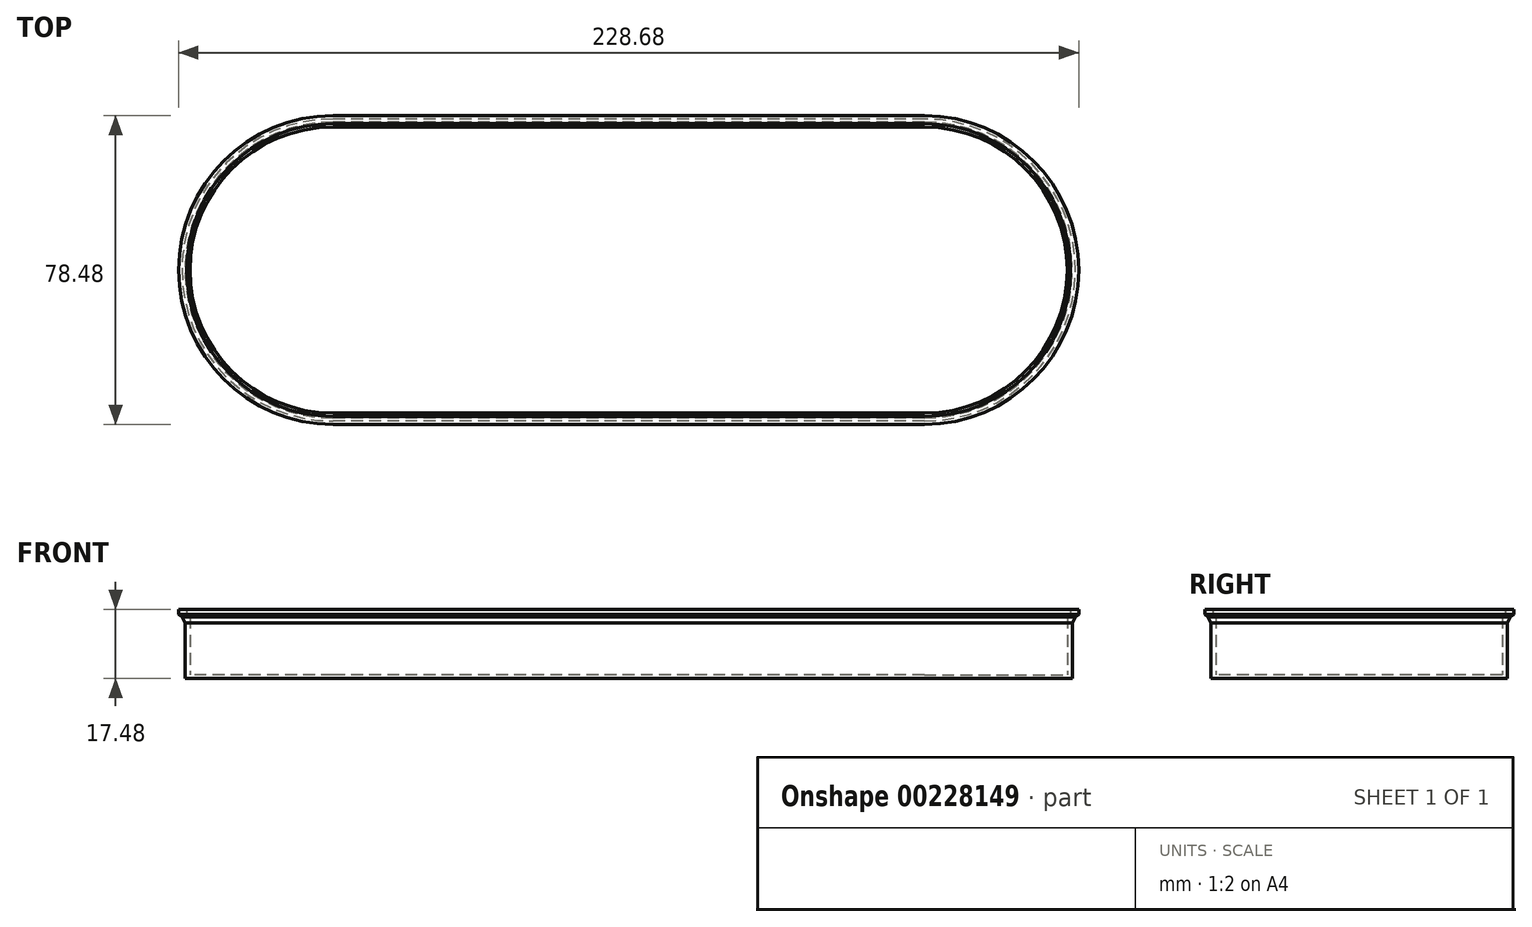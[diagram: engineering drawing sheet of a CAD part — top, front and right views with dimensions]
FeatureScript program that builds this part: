
annotation { "Feature Type Name" : "Feature", "Feature Type Description" : "" }
export const myFeature = defineFeature(function(context is Context, id is Id, definition is map)
    precondition{}
    {
        {
            assignVariable(context, id + "F0", {"name" : "Height", "anyValue" : 15});
        }
        {
            assignVariable(context, id + "F1", {"name" : "WallThickness", "anyValue" : 1.24});
        }
        {
            var Q0;
            Q0=qCreatedBy(makeId("Top.planeOp"),FACE);
            var sketch = newSketch(context, id + "F2", { "sketchPlane" : qUnion([Q0])});
            skLineSegment(sketch, "E0.bottom", {"start": v(75.1, 37.6) * mm, "end": v(-75.1, 37.6) * mm});
            skLineSegment(sketch, "E0.top", {"start": v(75.1, -37.6) * mm, "end": v(-75.1, -37.6) * mm});
            skLineSegment(sketch, "E0.left", {"start": v(75.1, 37.6) * mm, "end": v(75.1, -37.6) * mm});
            skLineSegment(sketch, "E0.right", {"start": v(-75.1, 37.6) * mm, "end": v(-75.1, -37.6) * mm});
            skPoint(sketch, "E0.middle", {"position": v(0, 0) * mm});
            skCircle(sketch, "E1", {"center": v(-75.1, 0) * mm, "radius": 37.6 * mm});
            skCircle(sketch, "E2", {"center": v(75.1, 0) * mm, "radius": 37.6 * mm});
            skSolve(sketch);
        }
        {
            var Q0;
            Q0=makeQuery(id+"F2.imprint","IMPRINT",FACE,{"disambiguationData":[TD([[makeQuery(id+"F2.imprint","IMPRINT",EDGE,{"derivedFrom":sQuery(id+"F2.wireOp",EDGE,"E0.bottom")}),1.0]])]});
            var Q1;
            {var subQ0=sQuery(id+"F2.wireOp",EDGE,"E0.left");Q1=makeQuery(id+"F2.imprint","IMPRINT",FACE,{"disambiguationData":[TD([[makeQuery(id+"F2.imprint","IMPRINT",EDGE,{"derivedFrom":subQ0}),-1.0]])]});}
            var Q2;
            {var subQ0=sQuery(id+"F2.wireOp",EDGE,"E0.right");Q2=makeQuery(id+"F2.imprint","IMPRINT",FACE,{"disambiguationData":[TD([[makeQuery(id+"F2.imprint","IMPRINT",EDGE,{"derivedFrom":subQ0}),-1.0]])]});}
            var Q3;
            {var subQ0=sQuery(id+"F2.wireOp",EDGE,"E0.right");Q3=makeQuery(id+"F2.imprint","IMPRINT",FACE,{"disambiguationData":[TD([[makeQuery(id+"F2.imprint","IMPRINT",EDGE,{"derivedFrom":subQ0}),1.0]])]});}
            var Q4;
            {var subQ0=sQuery(id+"F2.wireOp",EDGE,"E0.left");Q4=makeQuery(id+"F2.imprint","IMPRINT",FACE,{"disambiguationData":[TD([[makeQuery(id+"F2.imprint","IMPRINT",EDGE,{"derivedFrom":subQ0}),1.0]])]});}
            extrude(context, id + "F3", {"entities" : qUnion([Q0, Q1, Q2, Q3, Q4]), "offsetDistance" : 25 * mm, "depth" : (getVariable(context, 'Height')) * mm});
        }
        {
            var Q0;
            Q0=makeQuery(id+"F3.opExtrude","CAP_FACE",FACE,{"disambiguationData":[OSD([sQuery(id+"F2.wireOp",EDGE,"E0.bottom"),sQuery(id+"F2.wireOp",EDGE,"E0.top"),sQuery(id+"F2.wireOp",EDGE,"E0.left"),sQuery(id+"F2.wireOp",EDGE,"E0.right")])],"isStart":false});
            cPlane(context, id + "F4", {"entities" : qUnion([Q0]), "cplaneType" : CPlaneType.OFFSET, "offset" : (getVariable(context, 'WallThickness')) * mm, "width" : 150 * mm, "height" : 150 * mm});
        }
        {
            var Q0;
            Q0=qCreatedBy(id+"F4.planeOp",FACE);
            var sketch = newSketch(context, id + "F5", { "sketchPlane" : qUnion([Q0])});
            skLineSegment(sketch, "E3.0.0", {"start": v(-75.1, -37.6) * mm, "end": v(75.1, -37.6) * mm, "construction": true});
            skArc(sketch, "E3.0.1", {"start": v(75.1, -37.6) * mm, "mid": v(112.7, 0) * mm, "end": v(75.1, 37.6) * mm, "construction": true});
            skLineSegment(sketch, "E3.0.2", {"start": v(75.1, 37.6) * mm, "end": v(-75.1, 37.6) * mm, "construction": true});
            skArc(sketch, "E3.0.3", {"start": v(-75.1, 37.6) * mm, "mid": v(-112.7, 0) * mm, "end": v(-75.1, -37.6) * mm, "construction": true});
            skArc(sketch, "E4.0", {"start": v(-75.1, 38) * mm, "mid": v(-113.1, 0) * mm, "end": v(-75.1, -38) * mm, "construction": true});
            skLineSegment(sketch, "E4.1", {"start": v(75.1, 38) * mm, "end": v(-75.1, 38) * mm, "construction": true});
            skArc(sketch, "E4.2", {"start": v(75.1, -38) * mm, "mid": v(113.1, 0) * mm, "end": v(75.1, 38) * mm, "construction": true});
            skLineSegment(sketch, "E4.3", {"start": v(-75.1, -38) * mm, "end": v(75.1, -38) * mm, "construction": true});
            skArc(sketch, "E5.0", {"start": v(-75.1, 39.24) * mm, "mid": v(-114.34, 0) * mm, "end": v(-75.1, -39.24) * mm});
            skLineSegment(sketch, "E5.1", {"start": v(75.1, 39.24) * mm, "end": v(-75.1, 39.24) * mm});
            skArc(sketch, "E5.2", {"start": v(75.1, -39.24) * mm, "mid": v(114.34, 0) * mm, "end": v(75.1, 39.24) * mm});
            skLineSegment(sketch, "E5.3", {"start": v(-75.1, -39.24) * mm, "end": v(75.1, -39.24) * mm});
            skSolve(sketch);
        }
        {
            var Q1;
            Q1=makeQuery(id+"F3.opExtrude","CAP_FACE",FACE,{"disambiguationData":[OSD([sQuery(id+"F2.wireOp",EDGE,"E0.bottom"),sQuery(id+"F2.wireOp",EDGE,"E0.top"),sQuery(id+"F2.wireOp",EDGE,"E1"),sQuery(id+"F2.wireOp",EDGE,"E2")])],"isStart":false});
            var Q2;
            Q2=makeQuery(id+"F5.imprint","IMPRINT",FACE,{"disambiguationData":[TD([[makeQuery(id+"F5.imprint","IMPRINT",EDGE,{"derivedFrom":sQuery(id+"F5.wireOp",EDGE,"E5.0")}),1.0]])]});
            loft(context, id + "F6", {"operationType" : NewBodyOperationType.ADD, "sheetProfilesArray" : [{ "sheetProfileEntities" : qUnion([Q1]) }, { "sheetProfileEntities" : qUnion([Q2]) }]});
        }
        {
            var Q0;
            Q0=makeQuery(id+"F6.opLoft","CAP_FACE",FACE,{"disambiguationData":[OSD([makeQuery(id+"F5.imprint","IMPRINT",FACE,{"disambiguationData":[TD([[makeQuery(id+"F5.imprint","IMPRINT",EDGE,{"derivedFrom":sQuery(id+"F5.wireOp",EDGE,"E5.0")}),1.0]])]})])],"isStart":true});
            shell(context, id + "F7", {"entities" : qUnion([Q0]), "thickness" : (getVariable(context, 'WallThickness')) * mm});
        }
        {
            var Q0;
            Q0=makeQuery(id+"F6.opLoft","CAP_FACE",FACE,{"disambiguationData":[OSD([makeQuery(id+"F5.imprint","IMPRINT",FACE,{"disambiguationData":[TD([[makeQuery(id+"F5.imprint","IMPRINT",EDGE,{"derivedFrom":sQuery(id+"F5.wireOp",EDGE,"E5.0")}),1.0]])]})])],"isStart":true});
            extrude(context, id + "F8", {"entities" : qUnion([Q0]), "operationType" : NewBodyOperationType.ADD, "offsetDistance" : 25 * mm, "depth" : (getVariable(context, 'WallThickness')) * mm});
        }
        {
            var Q0;
            {var subQ0=sQuery(id+"F2.wireOp",EDGE,"E0.right");Q0=makeQuery(id+"F6.boolean.opBoolean","MERGE",EDGE,{"derivedFrom":[makeQuery(id+"F3.opExtrude","CAP_EDGE",EDGE,{"disambiguationData":[OSD([subQ0])],"isStart":false}),makeQuery(id+"F6.opLoft","MID_CAP_EDGE",EDGE,{"disambiguationData":[OSD([sQuery(id+"F2.wireOp",EDGE,"E0.bottom"),sQuery(id+"F2.wireOp",EDGE,"E0.top"),subQ0])],"capPos":1.0})]});}
            var Q1;
            {var subQ0=sQuery(id+"F2.wireOp",EDGE,"E0.top");Q1=makeQuery(id+"F6.boolean.opBoolean","MERGE",EDGE,{"derivedFrom":[makeQuery(id+"F3.opExtrude","CAP_EDGE",EDGE,{"disambiguationData":[OSD([subQ0])],"isStart":false}),makeQuery(id+"F6.opLoft","MID_CAP_EDGE",EDGE,{"disambiguationData":[OSD([subQ0,sQuery(id+"F2.wireOp",EDGE,"E0.left"),sQuery(id+"F2.wireOp",EDGE,"E0.right")])],"capPos":1.0})]});}
            var Q2;
            {var subQ0=sQuery(id+"F2.wireOp",EDGE,"E0.left");Q2=makeQuery(id+"F6.boolean.opBoolean","MERGE",EDGE,{"derivedFrom":[makeQuery(id+"F3.opExtrude","CAP_EDGE",EDGE,{"disambiguationData":[OSD([subQ0])],"isStart":false}),makeQuery(id+"F6.opLoft","MID_CAP_EDGE",EDGE,{"disambiguationData":[OSD([sQuery(id+"F2.wireOp",EDGE,"E0.bottom"),sQuery(id+"F2.wireOp",EDGE,"E0.top"),subQ0])],"capPos":1.0})]});}
            var Q3;
            {var subQ0=sQuery(id+"F2.wireOp",EDGE,"E0.bottom");Q3=makeQuery(id+"F6.boolean.opBoolean","MERGE",EDGE,{"derivedFrom":[makeQuery(id+"F3.opExtrude","CAP_EDGE",EDGE,{"disambiguationData":[OSD([subQ0])],"isStart":false}),makeQuery(id+"F6.opLoft","MID_CAP_EDGE",EDGE,{"disambiguationData":[OSD([subQ0,sQuery(id+"F2.wireOp",EDGE,"E0.left"),sQuery(id+"F2.wireOp",EDGE,"E0.right")])],"capPos":1.0})]});}
            chamfer(context, id + "F9", {"entities" : qUnion([Q0, Q1, Q2, Q3]), "width" : 2 * mm, "tangentPropagation" : true});
        }
        {
            var Q0;
            Q0=makeQuery(id+"F7.opShell","OFFSET_FACE",FACE,{"disambiguationData":[OSD([sQuery(id+"F2.wireOp",EDGE,"E0.bottom"),sQuery(id+"F2.wireOp",EDGE,"E0.top"),sQuery(id+"F2.wireOp",EDGE,"E1"),sQuery(id+"F2.wireOp",EDGE,"E2")])]});
            extrude(context, id + "F10", {"entities" : qUnion([Q0]), "operationType" : NewBodyOperationType.REMOVE, "oppositeDirection" : true, "depth" : 0.39 * mm, "offsetDistance" : 25 * mm});
        }
    });
